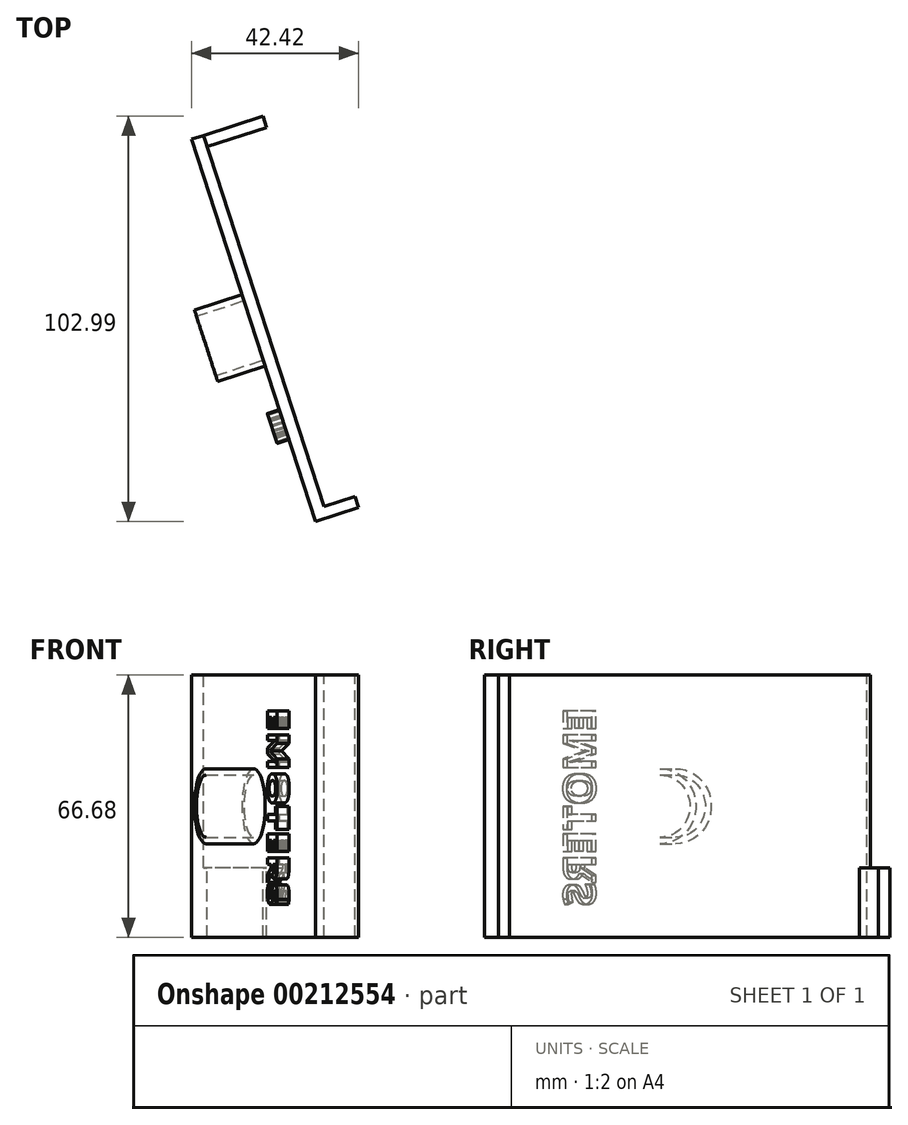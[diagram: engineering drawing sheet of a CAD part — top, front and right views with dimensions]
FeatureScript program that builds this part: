
annotation { "Feature Type Name" : "Feature", "Feature Type Description" : "" }
export const myFeature = defineFeature(function(context is Context, id is Id, definition is map)
    precondition{}
    {
        {
            var Q0;
            Q0=qCreatedBy(makeId("Top.planeOp"),FACE);
            var sketch = newSketch(context, id + "F0", { "sketchPlane" : qUnion([Q0])});
            skCircle(sketch, "E0", {"center": v(0, 0) * mm, "radius": 7.94 * mm});
            skCircle(sketch, "E1", {"center": v(0, 0) * mm, "radius": 9.53 * mm});
            skSolve(sketch);
        }
        {
            var Q0;
            Q0 = qSketchRegion(id + "F0", true);
            extrude(context, id + "F1", {"entities" : qUnion([Q0]), "depth" : 12.7 * mm});
        }
        {
            var Q0;
            Q0=qCreatedBy(makeId("Top.planeOp"),FACE);
            var sketch = newSketch(context, id + "F2", { "sketchPlane" : qUnion([Q0])});
            skLineSegment(sketch, "E2.bottom", {"start": v(-33.34, 51.05) * mm, "end": v(33.34, 51.05) * mm});
            skLineSegment(sketch, "E2.top", {"start": v(-33.34, -51.05) * mm, "end": v(33.34, -51.05) * mm});
            skLineSegment(sketch, "E2.left", {"start": v(-33.34, 51.05) * mm, "end": v(-33.34, -51.05) * mm});
            skLineSegment(sketch, "E2.right", {"start": v(33.34, 51.05) * mm, "end": v(33.34, -51.05) * mm});
            skPoint(sketch, "E2.middle", {"position": v(0, 0) * mm});
            skSolve(sketch);
        }
        {
            var Q0;
            Q0=makeQuery(id+"F2.imprint","IMPRINT",FACE,{"disambiguationData":[TD([[makeQuery(id+"F2.imprint","IMPRINT",EDGE,{"derivedFrom":sQuery(id+"F2.wireOp",EDGE,"E2.bottom")}),-1.0]])]});
            extrude(context, id + "F3", {"entities" : qUnion([Q0]), "operationType" : NewBodyOperationType.ADD, "oppositeDirection" : true, "depth" : 3.17 * mm});
        }
        {
            var Q0;
            Q0=makeQuery(id+"F3.opExtrude","CAP_FACE",FACE,{"disambiguationData":[OSD([sQuery(id+"F2.wireOp",EDGE,"E2.bottom"),sQuery(id+"F2.wireOp",EDGE,"E2.top"),sQuery(id+"F2.wireOp",EDGE,"E2.left"),sQuery(id+"F2.wireOp",EDGE,"E2.right")])],"isStart":false});
            var sketch = newSketch(context, id + "F4", { "sketchPlane" : qUnion([Q0])});
            skLineSegment(sketch, "E3.bottom", {"start": v(-33.34, 51.05) * mm, "end": v(33.34, 51.05) * mm});
            skLineSegment(sketch, "E3.top", {"start": v(-33.34, 48.04) * mm, "end": v(33.34, 48.04) * mm});
            skLineSegment(sketch, "E3.left", {"start": v(-33.34, 51.05) * mm, "end": v(-33.34, 48.04) * mm});
            skLineSegment(sketch, "E3.right", {"start": v(33.34, 51.05) * mm, "end": v(33.34, 48.04) * mm});
            skLineSegment(sketch, "E4.bottom", {"start": v(-33.34, -51.05) * mm, "end": v(-15.64, -51.05) * mm});
            skLineSegment(sketch, "E4.top", {"start": v(-33.34, -48.04) * mm, "end": v(-15.64, -48.04) * mm});
            skLineSegment(sketch, "E4.left", {"start": v(-33.34, -51.05) * mm, "end": v(-33.34, -48.04) * mm});
            skLineSegment(sketch, "E4.right", {"start": v(-15.64, -51.05) * mm, "end": v(-15.64, -48.04) * mm});
            skLineSegment(sketch, "E5.bottom", {"start": v(-33.34, -48.04) * mm, "end": v(-30.33, -48.04) * mm});
            skLineSegment(sketch, "E5.top", {"start": v(-33.34, -34.3) * mm, "end": v(-30.33, -34.3) * mm});
            skLineSegment(sketch, "E5.left", {"start": v(-33.34, -48.04) * mm, "end": v(-33.34, -34.3) * mm});
            skLineSegment(sketch, "E5.right", {"start": v(-30.33, -48.04) * mm, "end": v(-30.33, -34.3) * mm});
            skLineSegment(sketch, "E6.bottom", {"start": v(33.34, -51.05) * mm, "end": v(24.34, -51.05) * mm});
            skLineSegment(sketch, "E7.bottom", {"start": v(33.34, 48.04) * mm, "end": v(30.33, 48.04) * mm});
            skLineSegment(sketch, "E7.top", {"start": v(33.34, 34.3) * mm, "end": v(30.33, 34.3) * mm});
            skLineSegment(sketch, "E7.left", {"start": v(33.34, 48.04) * mm, "end": v(33.34, 34.3) * mm});
            skLineSegment(sketch, "E7.right", {"start": v(30.33, 48.04) * mm, "end": v(30.33, 34.3) * mm});
            skLineSegment(sketch, "E8.bottom", {"start": v(33.34, -51.05) * mm, "end": v(24.45, -51.05) * mm});
            skLineSegment(sketch, "E8.top", {"start": v(33.34, -48.04) * mm, "end": v(24.45, -48.04) * mm});
            skLineSegment(sketch, "E8.left", {"start": v(33.34, -51.05) * mm, "end": v(33.34, -48.04) * mm});
            skLineSegment(sketch, "E8.right", {"start": v(24.45, -51.05) * mm, "end": v(24.45, -48.04) * mm});
            skSolve(sketch);
        }
        {
            var Q0;
            Q0=makeQuery(id+"F4.imprint","IMPRINT",FACE,{"disambiguationData":[TD([[makeQuery(id+"F4.imprint","IMPRINT",EDGE,{"derivedFrom":sQuery(id+"F4.wireOp",EDGE,"E3.bottom")}),-1.0]])]});
            extrude(context, id + "F5", {"entities" : qUnion([Q0]), "operationType" : NewBodyOperationType.ADD, "depth" : 8.25 * mm});
        }
        {
            var Q0;
            Q0=makeQuery(id+"F4.imprint","IMPRINT",FACE,{"disambiguationData":[TD([[makeQuery(id+"F4.imprint","IMPRINT",EDGE,{"derivedFrom":sQuery(id+"F4.wireOp",EDGE,"E5.bottom")}),1.0]])]});
            var Q1;
            Q1=makeQuery(id+"F4.imprint","IMPRINT",FACE,{"disambiguationData":[TD([[makeQuery(id+"F4.imprint","IMPRINT",EDGE,{"derivedFrom":sQuery(id+"F4.wireOp",EDGE,"E4.bottom")}),1.0]])]});
            var Q2;
            Q2=makeQuery(id+"F4.imprint","IMPRINT",FACE,{"disambiguationData":[TD([[makeQuery(id+"F4.imprint","IMPRINT",EDGE,{"derivedFrom":sQuery(id+"F4.wireOp",EDGE,"E7.bottom")}),1.0]])]});
            var Q3;
            Q3=makeQuery(id+"F4.imprint","IMPRINT",FACE,{"disambiguationData":[TD([[makeQuery(id+"F4.imprint","IMPRINT",EDGE,{"derivedFrom":sQuery(id+"F4.wireOp",EDGE,"E8.bottom")}),1.0]])]});
            extrude(context, id + "F6", {"entities" : qUnion([Q0, Q1, Q2, Q3]), "operationType" : NewBodyOperationType.ADD, "depth" : 15.88 * mm});
        }
        {
            var Q0;
            {var subQ0=sQuery(id+"F2.wireOp",EDGE,"E2.left");var subQ1=sQuery(id+"F2.wireOp",EDGE,"E2.top");var subQ2=sQuery(id+"F2.wireOp",EDGE,"E2.bottom");var subQ3=sQuery(id+"F2.wireOp",EDGE,"E2.right");Q0=makeQuery(id+"F3.boolean.opBoolean","SPLIT",FACE,{"disambiguationData":[TD([makeQuery(id+"F1.opExtrude","SWEPT_FACE",FACE,{"disambiguationData":[OSD([sQuery(id+"F0.wireOp",EDGE,"E1")])]})])],"derivedFrom":makeQuery(id+"F3.opExtrude","CAP_FACE",FACE,{"disambiguationData":[OSD([subQ2,subQ1,subQ0,subQ3])],"isStart":true})});}
            var sketch = newSketch(context, id + "F7", { "sketchPlane" : qUnion([Q0])});
            skText(sketch, "E9", { "text": "EMOTERS", "fontName": "OpenSans-Bold.ttf"});
            const initialGuessF7  = {"E9": [0.0252, -0.02128, -1, 0, 0.00783]};
            skSetInitialGuess(sketch, initialGuessF7);
            skSolve(sketch);
        }
        {
            var Q0;
            Q0 = qSketchRegion(id + "F7", true);
            extrude(context, id + "F8", {"entities" : qUnion([Q0]), "operationType" : NewBodyOperationType.ADD, "depth" : 3.17 * mm});
        }
        {
            var Q0;
            Q0=makeQuery(id+"F1.opExtrude","SWEPT_BODY",BODY,{"disambiguationData":[OSD([sQuery(id+"F0.wireOp",EDGE,"E0"),sQuery(id+"F0.wireOp",EDGE,"E1")])]});
            var Q1;
            Q1=makeQuery(id+"F3.opExtrude","CAP_EDGE",EDGE,{"disambiguationData":[OSD([sQuery(id+"F2.wireOp",EDGE,"E2.left")])],"isStart":true});
            transform(context, id + "F9", {"entities" : qUnion([Q0]), "transformType" : TransformType.ROTATION, "transformAxis" : qUnion([Q1]), "angle" : 90 * degree, "makeCopy" : false});
        }
        {
            var Q0;
            Q0=makeQuery(id+"F1.opExtrude","SWEPT_BODY",BODY,{"disambiguationData":[OSD([sQuery(id+"F0.wireOp",EDGE,"E0"),sQuery(id+"F0.wireOp",EDGE,"E1")])]});
            var Q1;
            Q1=makeQuery(id+"F3.opExtrude","CAP_EDGE",EDGE,{"disambiguationData":[OSD([sQuery(id+"F2.wireOp",EDGE,"E2.top")])],"isStart":true});
            transform(context, id + "F10", {"entities" : qUnion([Q0]), "transformType" : TransformType.ROTATION, "transformAxis" : qUnion([Q1]), "angle" : 18 * degree, "makeCopy" : false});
        }
    });
